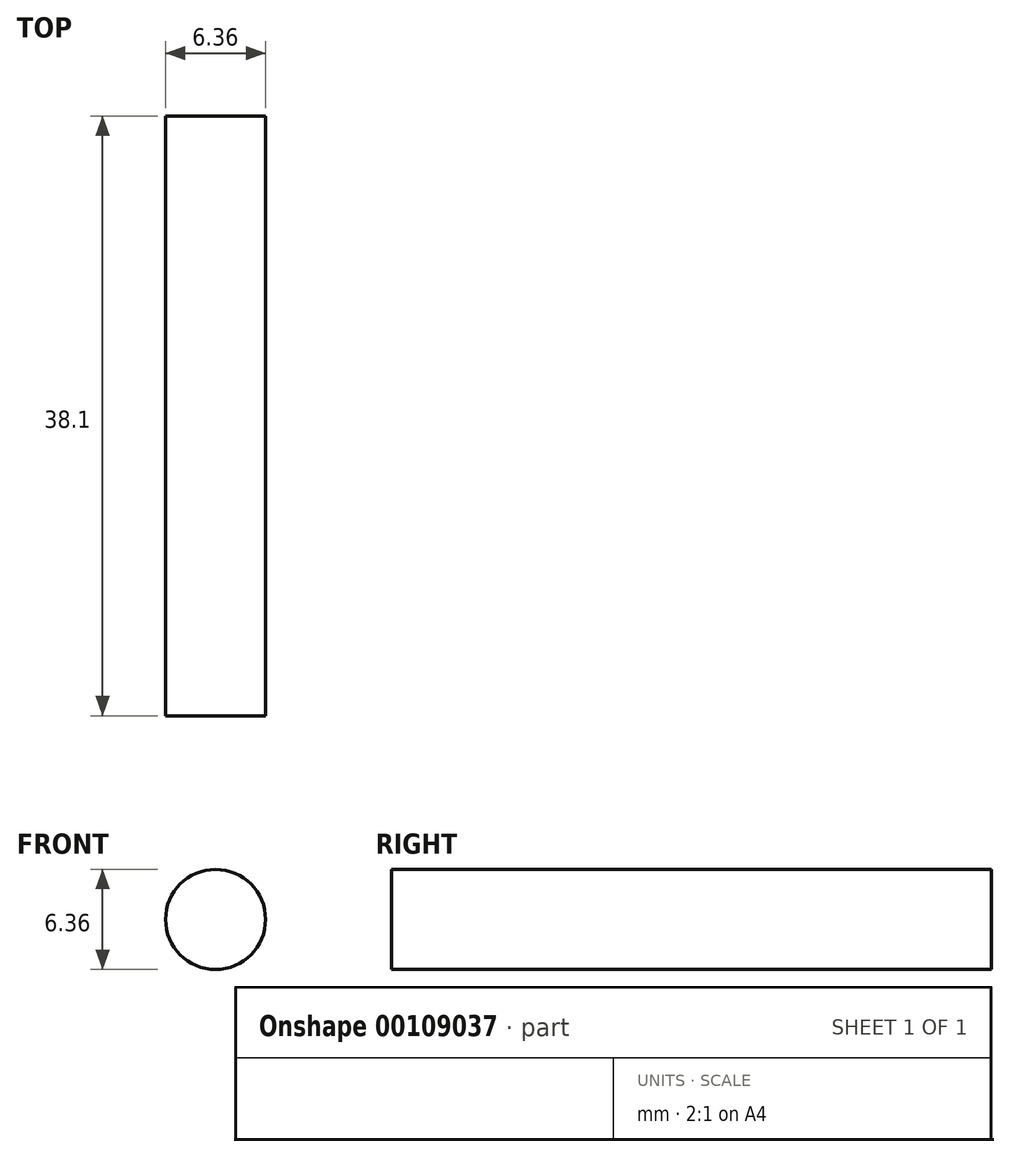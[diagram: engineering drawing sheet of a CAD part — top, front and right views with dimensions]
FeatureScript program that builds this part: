
annotation { "Feature Type Name" : "Feature", "Feature Type Description" : "" }
export const myFeature = defineFeature(function(context is Context, id is Id, definition is map)
    precondition{}
    {
        {
            var Q0;
            Q0=qCreatedBy(makeId("Front.planeOp"),FACE);
            var sketch = newSketch(context, id + "F0", { "sketchPlane" : qUnion([Q0])});
            skCircle(sketch, "E0", {"center": v(0, 0) * mm, "radius": 3.17 * mm});
            skSolve(sketch);
        }
        {
            var Q0;
            Q0=makeQuery(id+"F0.imprint","IMPRINT",FACE,{"disambiguationData":[TD([[makeQuery(id+"F0.imprint","IMPRINT",EDGE,{"derivedFrom":sQuery(id+"F0.wireOp",EDGE,"E0")}),1.0]])]});
            extrude(context, id + "F1", {"entities" : qUnion([Q0]), "depth" : 38.1 * mm});
        }
    });
